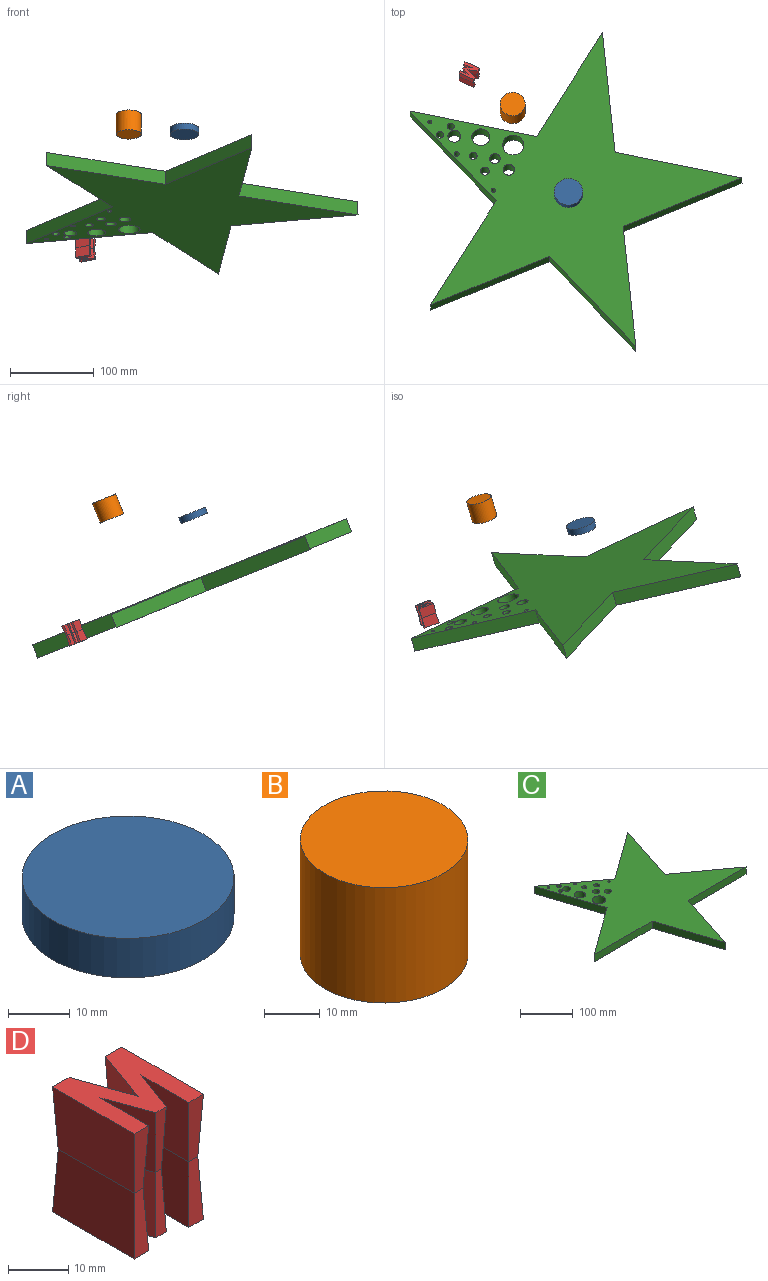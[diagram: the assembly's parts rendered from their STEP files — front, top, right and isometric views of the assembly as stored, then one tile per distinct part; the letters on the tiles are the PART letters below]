
ASSEMBLY  parts=4 mates=3
PART A: 3 faces, bbox 34.3x34.3x7.8 mm
  f0: cylinder r=17.15mm len=34.29mm, axis (0,0,-1), area 842.8mm2, adj f1,f2
  f1: plane 34.29x34.29mm, normal (0,0,1), area 923.6mm2, adj f0
  f2: plane 34.29x34.29mm, normal (0,0,-1), area 923.6mm2, adj f0
PART B: 3 faces, bbox 30.2x30.2x25.4 mm
  f0: cylinder r=15.08mm len=30.16mm, axis (0,0,-1), area 2407mm2, adj f1,f2
  f1: plane 30.16x30.16mm, normal (0,0,1), area 714.6mm2, adj f0
  f2: plane 30.16x30.16mm, normal (0,0,-1), area 714.6mm2, adj f0
PART C: 24 faces, bbox 406.6x386.7x16.9 mm
  f0: plane 125.63x91.28mm, normal (0.59,0.81,0), area 2621.2mm2, adj f1,f9,f10,f11
  f1: plane 147.69x47.99mm, normal (0.95,-0.31,0), area 2621.2mm2, adj f0,f2,f10,f11
  f2: plane 125.63x91.28mm, normal (-0.59,0.81,0), area 2621.2mm2, adj f1,f3,f10,f11
  f3: plane 125.63x91.28mm, normal (0.59,0.81,0), area 2621.2mm2, adj f2,f4,f10,f11
  f4: plane 147.69x47.99mm, normal (-0.95,-0.31,0), area 2621.2mm2, adj f3,f5,f10,f11
  f5: plane 125.63x91.28mm, normal (-0.59,0.81,0), area 2621.2mm2, adj f4,f6,f10,f11
  f6: plane 155.29x16.88mm, normal (0,-1,0), area 2621.2mm2, adj f5,f7,f10,f11
  f7: plane 147.69x47.99mm, normal (-0.95,-0.31,0), area 2621.2mm2, adj f6,f8,f10,f11
  f8: plane 147.69x47.99mm, normal (0.95,-0.31,0), area 2621.2mm2, adj f7,f9,f10,f11
  f9: plane 155.29x16.88mm, normal (0,-1,0), area 2621.2mm2, adj f0,f8,f10,f11
  f10: plane 406.56x386.66mm, normal (0,0,-1), area 49618.9mm2, adj f0,f1,f2,f3,f4,f5,f6,f7
  f11: plane 406.56x386.66mm, normal (0,0,1), area 49618.9mm2, adj f0,f1,f2,f3,f4,f5,f6,f7
  f12: cylinder r=12.83mm len=25.65mm, axis (0,0,1), area 1360.4mm2, adj f10,f11
  f13: cylinder r=10.79mm len=21.59mm, axis (0,0,1), area 1144.9mm2, adj f10,f11
  f14: cylinder r=6.9mm len=16.88mm, axis (0,0,1), area 731.4mm2, adj f10,f11
  f15: cylinder r=6.35mm len=16.88mm, axis (0,0,1), area 673.4mm2, adj f10,f11
  f16: cylinder r=7.67mm len=16.88mm, axis (0,0,1), area 813.5mm2, adj f10,f11
  f17: cylinder r=4.09mm len=16.88mm, axis (0,0,1), area 433.7mm2, adj f10,f11
  f18: cylinder r=4.2mm len=16.88mm, axis (0,0,1), area 445.8mm2, adj f10,f11
  f19: cylinder r=2.41mm len=16.88mm, axis (0,0,1), area 255.9mm2, adj f10,f11
  f20: cylinder r=2.82mm len=16.88mm, axis (0,0,1), area 299mm2, adj f10,f11
  f21: cylinder r=5.18mm len=16.88mm, axis (0,0,1), area 549.5mm2, adj f10,f11
  f22: cylinder r=4.6mm len=16.88mm, axis (0,0,1), area 487.6mm2, adj f10,f11
  f23: cylinder r=2.5mm len=16.88mm, axis (0,0,1), area 265.3mm2, adj f10,f11
PART D: 46 faces, bbox 16.5x19.5x30.8 mm
  f0: plane 12.59x4.51mm, normal (-0.94,-0.33,-0.05), area 28.3mm2, adj f1,f18,f19,f26
  f1: bspline ~15.24x5.32mm, area 41.4mm2, adj f0,f4,f18,f19,f20,f25
  f2: bspline ~15.24x5.33mm, area 40.9mm2, adj f3,f4,f14,f15,f16,f24
  f3: plane 12.42x4.56mm, normal (0.94,-0.33,-0.05), area 27.6mm2, adj f2,f15,f16,f23
  f4: plane 19.21x16.26mm, normal (0,0,1), area 210.7mm2, adj f1,f2,f5,f6,f7,f9,f10,f11
  f5: plane 12.7x3.86mm, normal (0,1,-0.05), area 41.9mm2, adj f4,f6,f22,f44
  f6: plane 12.7x10.22mm, normal (0.94,0.34,-0.05), area 132.1mm2, adj f4,f5,f7,f43
  f7: bspline ~15.24x4.02mm, area 39.7mm2, adj f4,f6,f8,f9,f42
  f8: plane 1.63x0.12mm, normal (0,1,-0.05), area 0.1mm2, adj f7,f9,f41
  f9: bspline ~15.24x4.02mm, area 39.6mm2, adj f4,f7,f8,f10,f40
  f10: plane 12.7x10.22mm, normal (-0.94,0.34,-0.05), area 132mm2, adj f4,f9,f11,f39
  f11: plane 12.7x3.86mm, normal (0,1,-0.05), area 41.9mm2, adj f4,f10,f12,f38
  f12: plane 19.19x12.7mm, normal (1,0,-0.05), area 235.6mm2, adj f4,f11,f13,f37
  f13: plane 12.7x3.45mm, normal (0,-1,-0.05), area 35.4mm2, adj f4,f12,f14,f36
  f14: plane 12.7x10.56mm, normal (-1,0,-0.05), area 130mm2, adj f2,f4,f13,f35
  f15: plane 1.05x0.1mm, normal (0,-1,-0.05), area 0.1mm2, adj f2,f3,f34
  f16: plane 12.7x9.95mm, normal (0.94,-0.34,-0.05), area 128.6mm2, adj f2,f3,f4,f17,f33
  f17: plane 12.7x2.44mm, normal (0,-1,-0.05), area 25.1mm2, adj f4,f16,f18,f32
  f18: plane 12.7x9.95mm, normal (-0.94,-0.34,-0.05), area 128.6mm2, adj f0,f1,f4,f17,f31
  f19: plane 1.06x0.1mm, normal (0,-1,-0.05), area 0.1mm2, adj f0,f1,f30
  f20: plane 12.7x10.56mm, normal (1,0,-0.05), area 130mm2, adj f1,f4,f21,f29
  f21: plane 12.7x3.38mm, normal (0,-1,-0.05), area 34.5mm2, adj f4,f20,f22,f28
  f22: plane 19.19x12.7mm, normal (-1,0,-0.05), area 235.6mm2, adj f4,f5,f21,f27
  f23: plane 12.42x4.56mm, normal (0.94,-0.33,0.05), area 27.6mm2, adj f3,f24,f33,f34
  f24: bspline ~15.24x5.33mm, area 40.9mm2, adj f2,f23,f33,f34,f35,f45
  f25: bspline ~15.24x5.32mm, area 41.4mm2, adj f1,f26,f29,f30,f31,f45
  f26: plane 12.59x4.51mm, normal (-0.94,-0.33,0.05), area 28.3mm2, adj f0,f25,f30,f31
  f27: plane 19.19x12.7mm, normal (-1,0,0.05), area 235.6mm2, adj f22,f28,f44,f45
  f28: plane 12.7x3.38mm, normal (0,-1,0.05), area 34.5mm2, adj f21,f27,f29,f45
  f29: plane 12.7x10.56mm, normal (1,0,0.05), area 130mm2, adj f20,f25,f28,f45
  f30: plane 1.06x0.1mm, normal (0,-1,0.05), area 0.1mm2, adj f19,f25,f26
  f31: plane 12.7x9.95mm, normal (-0.94,-0.34,0.05), area 128.6mm2, adj f18,f25,f26,f32,f45
  f32: plane 12.7x2.44mm, normal (0,-1,0.05), area 25.1mm2, adj f17,f31,f33,f45
  f33: plane 12.7x9.95mm, normal (0.94,-0.34,0.05), area 128.6mm2, adj f16,f23,f24,f32,f45
  f34: plane 1.05x0.1mm, normal (0,-1,0.05), area 0.1mm2, adj f15,f23,f24
  f35: plane 12.7x10.56mm, normal (-1,0,0.05), area 130mm2, adj f14,f24,f36,f45
  f36: plane 12.7x3.45mm, normal (0,-1,0.05), area 35.4mm2, adj f13,f35,f37,f45
  f37: plane 19.19x12.7mm, normal (1,0,0.05), area 235.6mm2, adj f12,f36,f38,f45
  f38: plane 12.7x3.86mm, normal (0,1,0.05), area 41.9mm2, adj f11,f37,f39,f45
  f39: plane 12.7x10.22mm, normal (-0.94,0.34,0.05), area 132mm2, adj f10,f38,f40,f45
  f40: bspline ~15.24x4.02mm, area 39.6mm2, adj f9,f39,f41,f42,f45
  f41: plane 1.63x0.12mm, normal (0,1,0.05), area 0.1mm2, adj f8,f40,f42
  f42: bspline ~15.24x4.02mm, area 39.7mm2, adj f7,f40,f41,f43,f45
  f43: plane 12.7x10.22mm, normal (0.94,0.34,0.05), area 132.1mm2, adj f6,f42,f44,f45
  f44: plane 12.7x3.86mm, normal (0,1,0.05), area 41.9mm2, adj f5,f27,f43,f45
  f45: plane 19.21x16.26mm, normal (0,0,-1), area 210.7mm2, adj f24,f25,f27,f28,f29,f31,f32,f33
PLACE A rot(axis=(1,0.05,-0.01),158.1deg) t=(147.74,-350.99,-7.64)mm
PLACE B rot(axis=(1,0.05,-0.01),158.1deg) t=(152.94,-427.79,82.31)mm
PLACE C rot(axis=(0.74,-0.67,0.13),164deg) t=(201.06,-415.24,-81.83)mm
PLACE D rot(axis=(0.84,0.53,-0.1),161.3deg) t=(85.27,-224.13,-145.6)mm
MATE slider C.f12 <-> B.f0  axis (0.01,-0.37,-0.93) through (140.19,-355.95,-106.01)mm
MATE planar C.f13 <-> D.f4  axis (0.01,-0.37,-0.93) through (101.33,-346.67,-109.96)mm
MATE slider A.f0 <-> C.f10  axis (-0.01,0.37,0.93) through (206.11,-405.9,14.76)mm
